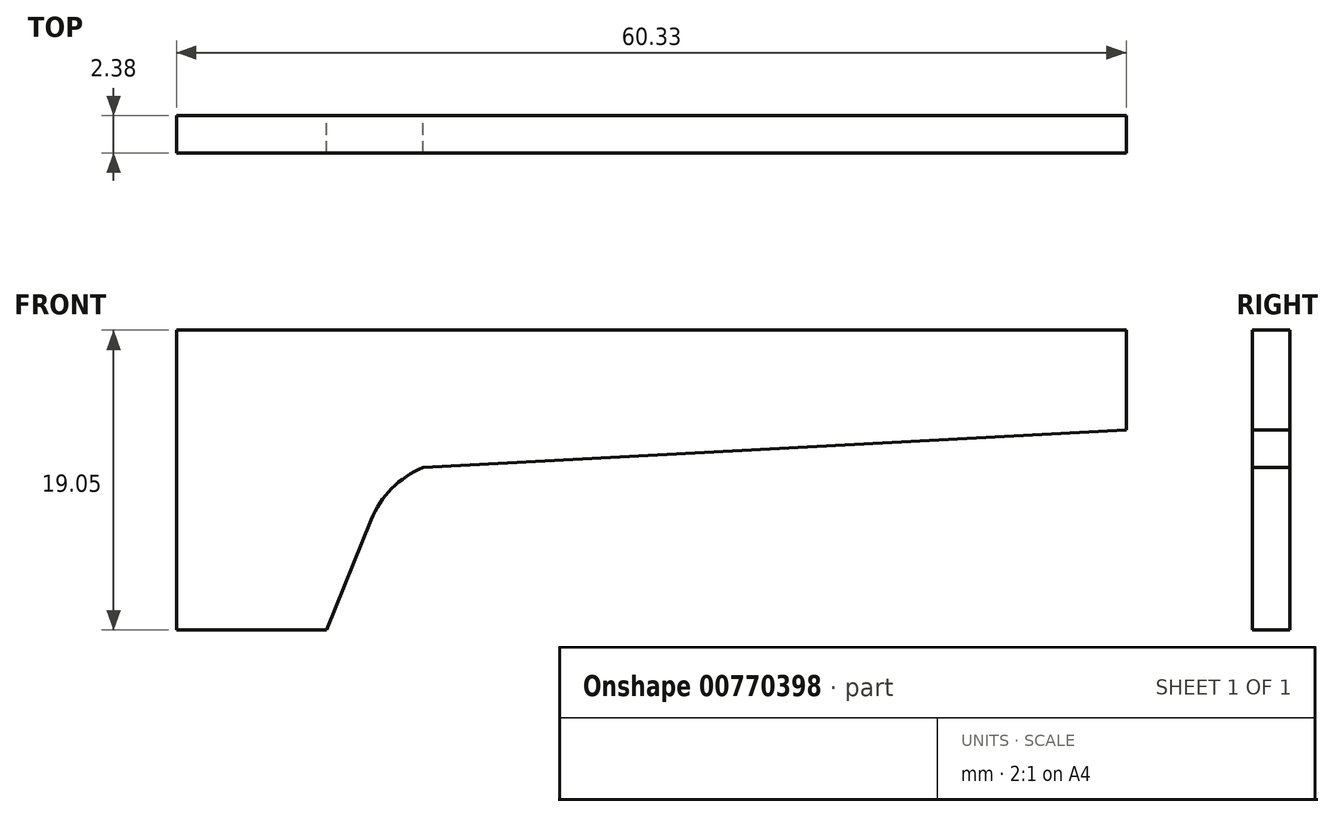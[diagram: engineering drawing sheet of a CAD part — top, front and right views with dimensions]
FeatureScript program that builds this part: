
annotation { "Feature Type Name" : "Feature", "Feature Type Description" : "" }
export const myFeature = defineFeature(function(context is Context, id is Id, definition is map)
    precondition{}
    {
        {
            var Q0;
            Q0=qCreatedBy(makeId("Front.planeOp"),FACE);
            var sketch = newSketch(context, id + "F0", { "sketchPlane" : qUnion([Q0])});
            skLineSegment(sketch, "E0.top", {"start": v(0, 19.05) * mm, "end": v(60.33, 19.05) * mm});
            skLineSegment(sketch, "E0.left", {"start": v(0, 0) * mm, "end": v(0, 19.05) * mm});
            skLineSegment(sketch, "E1", {"start": v(9.53, 0) * mm, "end": v(12.36, 7) * mm});
            skLineSegment(sketch, "E2", {"start": v(60.33, 12.7) * mm, "end": v(15.66, 10.32) * mm});
            skLineSegment(sketch, "E3", {"start": v(9.53, 0) * mm, "end": v(0, 0) * mm});
            skLineSegment(sketch, "E4", {"start": v(60.33, 12.7) * mm, "end": v(60.33, 19.05) * mm});
            skArc(sketch, "E5", {"start": v(15.66, 10.32) * mm, "mid": v(13.68, 8.99) * mm, "end": v(12.36, 7) * mm});
            skSolve(sketch);
        }
        {
            var Q0;
            Q0 = qSketchRegion(id + "F0", true);
            extrude(context, id + "F1", {"entities" : qUnion([Q0]), "depth" : 2.38 * mm, "offsetDistance" : 25.4 * mm});
        }
    });
